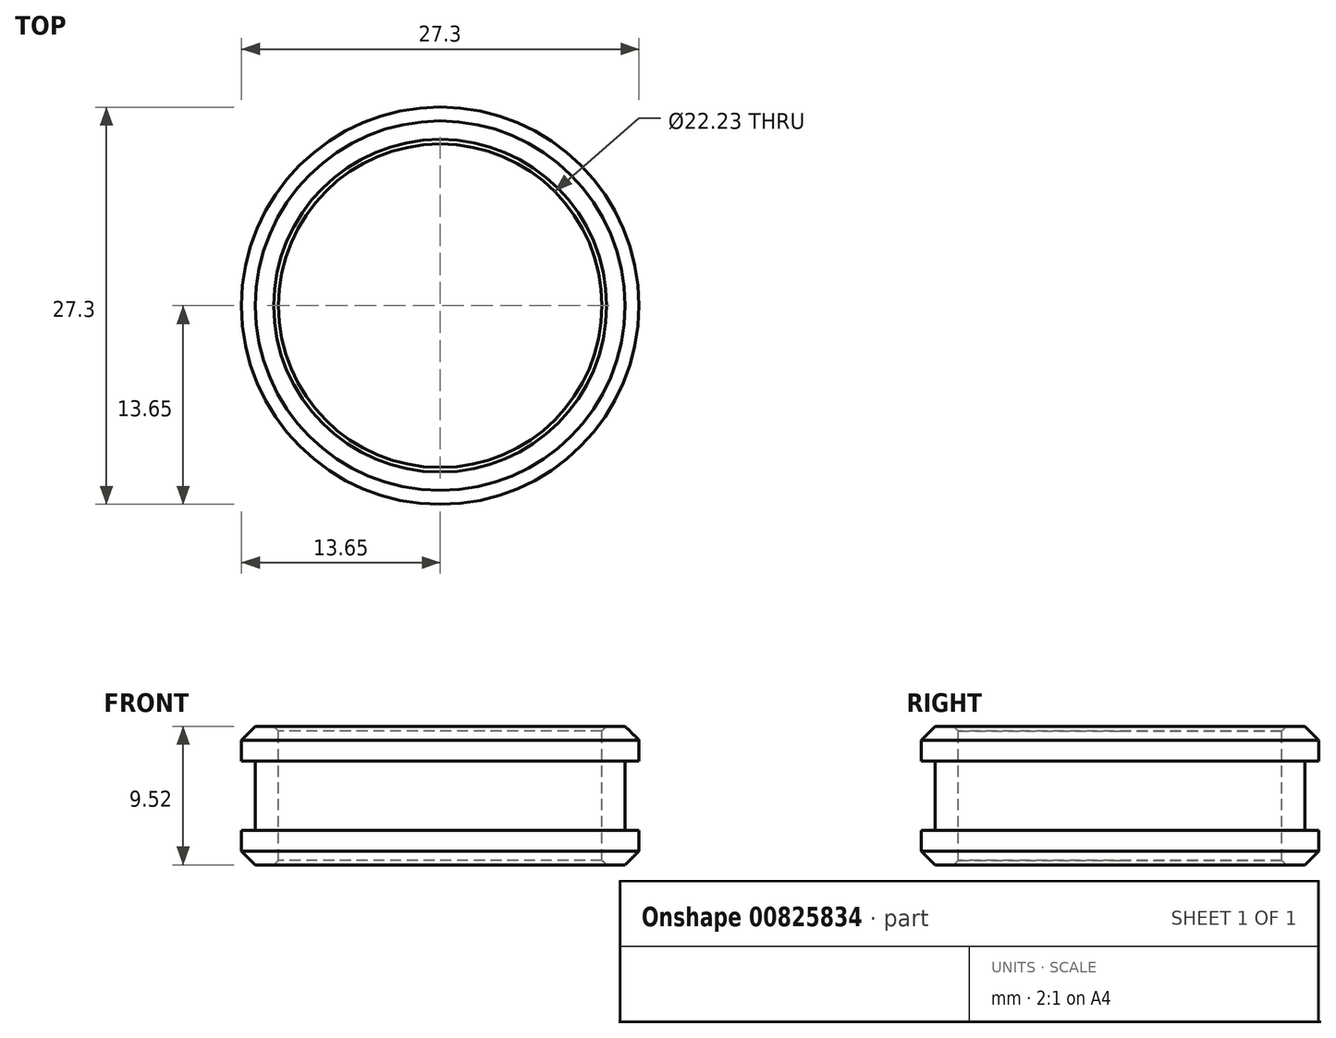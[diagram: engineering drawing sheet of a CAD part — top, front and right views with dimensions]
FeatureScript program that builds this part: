
annotation { "Feature Type Name" : "Feature", "Feature Type Description" : "" }
export const myFeature = defineFeature(function(context is Context, id is Id, definition is map)
    precondition{}
    {
        {
            var Q0;
            Q0=qCreatedBy(makeId("Front.planeOp"),FACE);
            var sketch = newSketch(context, id + "F0", { "sketchPlane" : qUnion([Q0])});
            skLineSegment(sketch, "E0", {"start": v(0, 4.76) * mm, "end": v(0, -4.76) * mm, "construction": true});
            skLineSegment(sketch, "E1.bottom", {"start": v(-11.11, 4.76) * mm, "end": v(-13.65, 4.76) * mm});
            skLineSegment(sketch, "E1.top", {"start": v(-11.11, -4.76) * mm, "end": v(-13.65, -4.76) * mm});
            skLineSegment(sketch, "E1.left", {"start": v(-11.11, 4.76) * mm, "end": v(-11.11, -4.76) * mm});
            skLineSegment(sketch, "E1.right", {"start": v(-13.65, 4.76) * mm, "end": v(-13.65, -4.76) * mm});
            skPoint(sketch, "E2", {"position": v(0, 0) * mm});
            skSolve(sketch);
        }
        {
            var Q0;
            Q0=makeQuery(id+"F0.imprint","IMPRINT",FACE,{"disambiguationData":[TD([[makeQuery(id+"F0.imprint","IMPRINT",EDGE,{"derivedFrom":sQuery(id+"F0.wireOp",EDGE,"E1.bottom")}),1.0]])]});
            var Q1;
            Q1=sQuery(id+"F0.wireOp",EDGE,"E0");
            revolve(context, id + "F1", {"surfaceOperationType" : NewSurfaceOperationType.NEW, "entities" : qUnion([Q0]), "axis" : qUnion([Q1]), "revolveType" : RevolveType.FULL});
        }
        {
            var Q0;
            Q0=makeQuery(id+"F1.opRevolve","SWEPT_EDGE",EDGE,{"disambiguationData":[OSD([sQuery(id+"F0.wireOp",EDGE,"E1.bottom"),sQuery(id+"F0.wireOp",EDGE,"E1.left")])]});
            var Q1;
            Q1=makeQuery(id+"F1.opRevolve","SWEPT_EDGE",EDGE,{"disambiguationData":[OSD([sQuery(id+"F0.wireOp",EDGE,"E1.top"),sQuery(id+"F0.wireOp",EDGE,"E1.left")])]});
            chamfer(context, id + "F2", {"entities" : qUnion([Q0, Q1]), "width" : 0.32 * mm, "tangentPropagation" : true});
        }
        {
            var Q0;
            Q0=makeQuery(id+"F1.opRevolve","SWEPT_EDGE",EDGE,{"disambiguationData":[OSD([sQuery(id+"F0.wireOp",EDGE,"E1.top"),sQuery(id+"F0.wireOp",EDGE,"E1.right")])]});
            var Q1;
            Q1=makeQuery(id+"F1.opRevolve","SWEPT_EDGE",EDGE,{"disambiguationData":[OSD([sQuery(id+"F0.wireOp",EDGE,"E1.bottom"),sQuery(id+"F0.wireOp",EDGE,"E1.right")])]});
            chamfer(context, id + "F3", {"entities" : qUnion([Q0, Q1]), "width" : 0.95 * mm, "tangentPropagation" : true});
        }
        {
            var Q0;
            Q0=qCreatedBy(makeId("Right.planeOp"),FACE);
            var sketch = newSketch(context, id + "F4", { "sketchPlane" : qUnion([Q0])});
            skLineSegment(sketch, "E3.bottom", {"start": v(14.96, 2.38) * mm, "end": v(12.7, 2.38) * mm});
            skLineSegment(sketch, "E3.top", {"start": v(14.96, -2.38) * mm, "end": v(12.7, -2.38) * mm});
            skLineSegment(sketch, "E3.left", {"start": v(14.96, 2.38) * mm, "end": v(14.96, -2.38) * mm});
            skLineSegment(sketch, "E3.right", {"start": v(12.7, 2.38) * mm, "end": v(12.7, -2.38) * mm});
            skPoint(sketch, "E3.middle", {"position": v(13.83, 0) * mm});
            skLineSegment(sketch, "E4", {"start": v(0, 9.1) * mm, "end": v(0, -9.87) * mm, "construction": true});
            skSolve(sketch);
        }
        {
            var Q0;
            Q0=makeQuery(id+"F4.imprint","IMPRINT",FACE,{"disambiguationData":[TD([[makeQuery(id+"F4.imprint","IMPRINT",EDGE,{"derivedFrom":sQuery(id+"F4.wireOp",EDGE,"E3.bottom")}),1.0]])]});
            var Q1;
            Q1=sQuery(id+"F4.wireOp",EDGE,"E4");
            revolve(context, id + "F5", {"operationType" : NewBodyOperationType.REMOVE, "surfaceOperationType" : NewSurfaceOperationType.NEW, "entities" : qUnion([Q0]), "axis" : qUnion([Q1]), "revolveType" : RevolveType.FULL, "oppositeDirection" : true});
        }
    });
